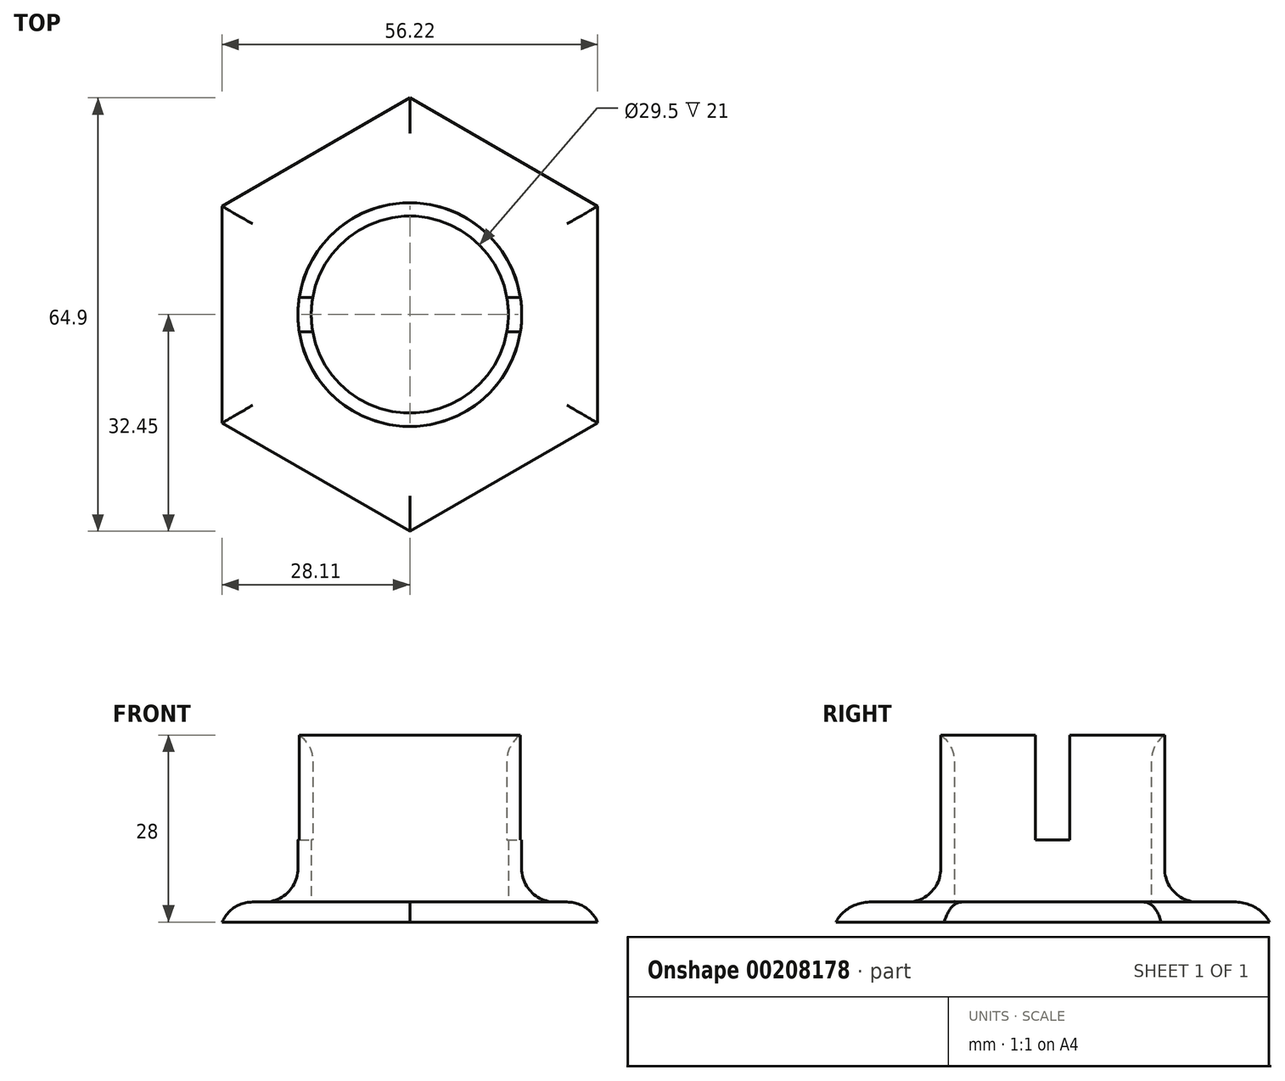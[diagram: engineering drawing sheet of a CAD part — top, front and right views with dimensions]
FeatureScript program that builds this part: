
annotation { "Feature Type Name" : "Feature", "Feature Type Description" : "" }
export const myFeature = defineFeature(function(context is Context, id is Id, definition is map)
    precondition{}
    {
        {
            var Q0;
            Q0=qCreatedBy(makeId("Top.planeOp"),FACE);
            var sketch = newSketch(context, id + "F0", { "sketchPlane" : qUnion([Q0])});
            skCircle(sketch, "E0.cCircle", {"center": v(0, 0) * mm, "radius": 25.98 * mm, "construction": true});
            skLineSegment(sketch, "E0.0", {"start": v(0, 30) * mm, "end": v(25.98, 15) * mm});
            skLineSegment(sketch, "E0.1", {"start": v(25.98, 15) * mm, "end": v(25.98, -15) * mm});
            skLineSegment(sketch, "E0.2", {"start": v(25.98, -15) * mm, "end": v(0, -30) * mm});
            skLineSegment(sketch, "E0.3", {"start": v(0, -30) * mm, "end": v(-25.98, -15) * mm});
            skLineSegment(sketch, "E0.4", {"start": v(-25.98, -15) * mm, "end": v(-25.98, 15) * mm});
            skLineSegment(sketch, "E0.5", {"start": v(-25.98, 15) * mm, "end": v(0, 30) * mm});
            skPoint(sketch, "E0.0.midPoint", {"position": v(13, 22.5) * mm});
            skCircle(sketch, "E1", {"center": v(0, 0) * mm, "radius": 14.75 * mm});
            skCircle(sketch, "E2.0", {"center": v(0, 0) * mm, "radius": 16.75 * mm});
            skSolve(sketch);
        }
        {
            var Q0;
            Q0=makeQuery(id+"F0.imprint","IMPRINT",FACE,{"disambiguationData":[TD([[makeQuery(id+"F0.imprint","IMPRINT",EDGE,{"derivedFrom":sQuery(id+"F0.wireOp",EDGE,"E1")}),-1.0]])]});
            extrude(context, id + "F1", {"entities" : qUnion([Q0]), "depth" : 25 * mm});
        }
        {
            var Q0;
            Q0=makeQuery(id+"F0.imprint","IMPRINT",FACE,{"disambiguationData":[TD([[makeQuery(id+"F0.imprint","IMPRINT",EDGE,{"derivedFrom":sQuery(id+"F0.wireOp",EDGE,"E0.0")}),-1.0]])]});
            var sketch = newSketch(context, id + "F2", { "sketchPlane" : qUnion([Q0])});
            skCircle(sketch, "E3.cCircle", {"center": v(0, 0) * mm, "radius": 28.1 * mm, "construction": true});
            skLineSegment(sketch, "E3.0", {"start": v(28.1, 16.23) * mm, "end": v(28.1, -16.23) * mm});
            skLineSegment(sketch, "E3.1", {"start": v(28.1, -16.23) * mm, "end": v(0, -32.45) * mm});
            skLineSegment(sketch, "E3.2", {"start": v(0, -32.45) * mm, "end": v(-28.1, -16.23) * mm});
            skLineSegment(sketch, "E3.3", {"start": v(-28.1, -16.23) * mm, "end": v(-28.1, 16.23) * mm});
            skLineSegment(sketch, "E3.4", {"start": v(-28.1, 16.23) * mm, "end": v(0, 32.45) * mm});
            skLineSegment(sketch, "E3.5", {"start": v(0, 32.45) * mm, "end": v(28.1, 16.23) * mm});
            skPoint(sketch, "E3.0.midPoint", {"position": v(28.1, 0) * mm});
            skSolve(sketch);
        }
        {
            var Q0;
            Q0 = qSketchRegion(id + "F2", true);
            extrude(context, id + "F3", {"entities" : qUnion([Q0]), "operationType" : NewBodyOperationType.ADD, "oppositeDirection" : true, "depth" : 3 * mm});
        }
        {
            var Q0;
            Q0=makeQuery(id+"F1.opExtrude","CAP_EDGE",EDGE,{"disambiguationData":[OSD([sQuery(id+"F0.wireOp",EDGE,"E2.0")])],"isStart":true});
            var Q1;
            {var subQ0=sQuery(id+"F2.wireOp",EDGE,"E3.2");var subQ1=sQuery(id+"F2.wireOp",EDGE,"E3.1");var subQ2=sQuery(id+"F2.wireOp",EDGE,"E3.0");var subQ3=sQuery(id+"F2.wireOp",EDGE,"E3.3");var subQ4=sQuery(id+"F2.wireOp",EDGE,"E3.4");var subQ5=sQuery(id+"F2.wireOp",EDGE,"E3.5");Q1=makeQuery(id+"F3.boolean.opBoolean","SPLIT",FACE,{"disambiguationData":[TD([makeQuery(id+"F1.opExtrude","SWEPT_FACE",FACE,{"disambiguationData":[OSD([sQuery(id+"F0.wireOp",EDGE,"E2.0")])]})])],"derivedFrom":makeQuery(id+"F3.opExtrude","CAP_FACE",FACE,{"disambiguationData":[OSD([subQ2,subQ1,subQ0,subQ3,subQ4,subQ5])],"isStart":true})});}
            fillet(context, id + "F4", {"entities" : qUnion([Q0, Q1]), "radius" : 5 * mm, "tangentPropagation" : true, "allowEdgeOverflow" : false});
        }
        {
            var Q0;
            Q0=qCreatedBy(makeId("Right.planeOp"),FACE);
            var sketch = newSketch(context, id + "F5", { "sketchPlane" : qUnion([Q0])});
            skLineSegment(sketch, "E4.bottom", {"start": v(2.57, 9.29) * mm, "end": v(0, 9.29) * mm});
            skLineSegment(sketch, "E4.top", {"start": v(2.57, 27.28) * mm, "end": v(0, 27.28) * mm});
            skLineSegment(sketch, "E4.left", {"start": v(2.57, 9.29) * mm, "end": v(2.57, 27.28) * mm});
            skLineSegment(sketch, "E4.right", {"start": v(0, 9.29) * mm, "end": v(0, 27.28) * mm});
            skLineSegment(sketch, "E5.MirrorCS", {"start": v(-2.57, 9.29) * mm, "end": v(-2.57, 27.28) * mm});
            skLineSegment(sketch, "E6.MirrorCS", {"start": v(-2.57, 9.29) * mm, "end": v(0, 9.29) * mm});
            skLineSegment(sketch, "E7.MirrorCS", {"start": v(-2.57, 27.28) * mm, "end": v(0, 27.28) * mm});
            skSolve(sketch);
        }
        {
            var Q0;
            Q0=makeQuery(id+"F5.imprint","IMPRINT",FACE,{"disambiguationData":[TD([[makeQuery(id+"F5.imprint","IMPRINT",EDGE,{"derivedFrom":sQuery(id+"F5.wireOp",EDGE,"E4.bottom")}),-1.0]])]});
            var Q1;
            Q1=makeQuery(id+"F5.imprint","IMPRINT",FACE,{"disambiguationData":[TD([[makeQuery(id+"F5.imprint","IMPRINT",EDGE,{"derivedFrom":sQuery(id+"F5.wireOp",EDGE,"E4.right")}),1.0]])]});
            extrude(context, id + "F6", {"entities" : qUnion([Q0, Q1]), "operationType" : NewBodyOperationType.REMOVE, "oppositeDirection" : true, "depth" : 25 * mm, "hasSecondDirection" : true, "secondDirectionOppositeDirection" : false, "secondDirectionDepth" : 25 * mm});
        }
        {
            var Q0;
            {var subQ0=sQuery(id+"F0.wireOp",EDGE,"E1");Q0=makeQuery(id+"F6.boolean.opBoolean","SPLIT",EDGE,{"disambiguationData":[TD([makeQuery(id+"F6.opExtrude","SWEPT_FACE",FACE,{"disambiguationData":[OSD([sQuery(id+"F5.wireOp",EDGE,"E5.MirrorCS")])]})])],"derivedFrom":makeQuery(id+"F1.opExtrude","CAP_EDGE",EDGE,{"disambiguationData":[OSD([subQ0])],"isStart":false})});}
            var Q1;
            {var subQ0=sQuery(id+"F0.wireOp",EDGE,"E1");Q1=makeQuery(id+"F6.boolean.opBoolean","SPLIT",EDGE,{"disambiguationData":[TD([makeQuery(id+"F6.opExtrude","SWEPT_FACE",FACE,{"disambiguationData":[OSD([sQuery(id+"F5.wireOp",EDGE,"E4.left")])]})])],"derivedFrom":makeQuery(id+"F1.opExtrude","CAP_EDGE",EDGE,{"disambiguationData":[OSD([subQ0])],"isStart":false})});}
            fillet(context, id + "F7", {"entities" : qUnion([Q0, Q1]), "radius" : 5 * mm, "tangentPropagation" : true, "rho" : 0.5, "crossSection" : FilletCrossSection.CONIC, "allowEdgeOverflow" : false});
        }
    });
